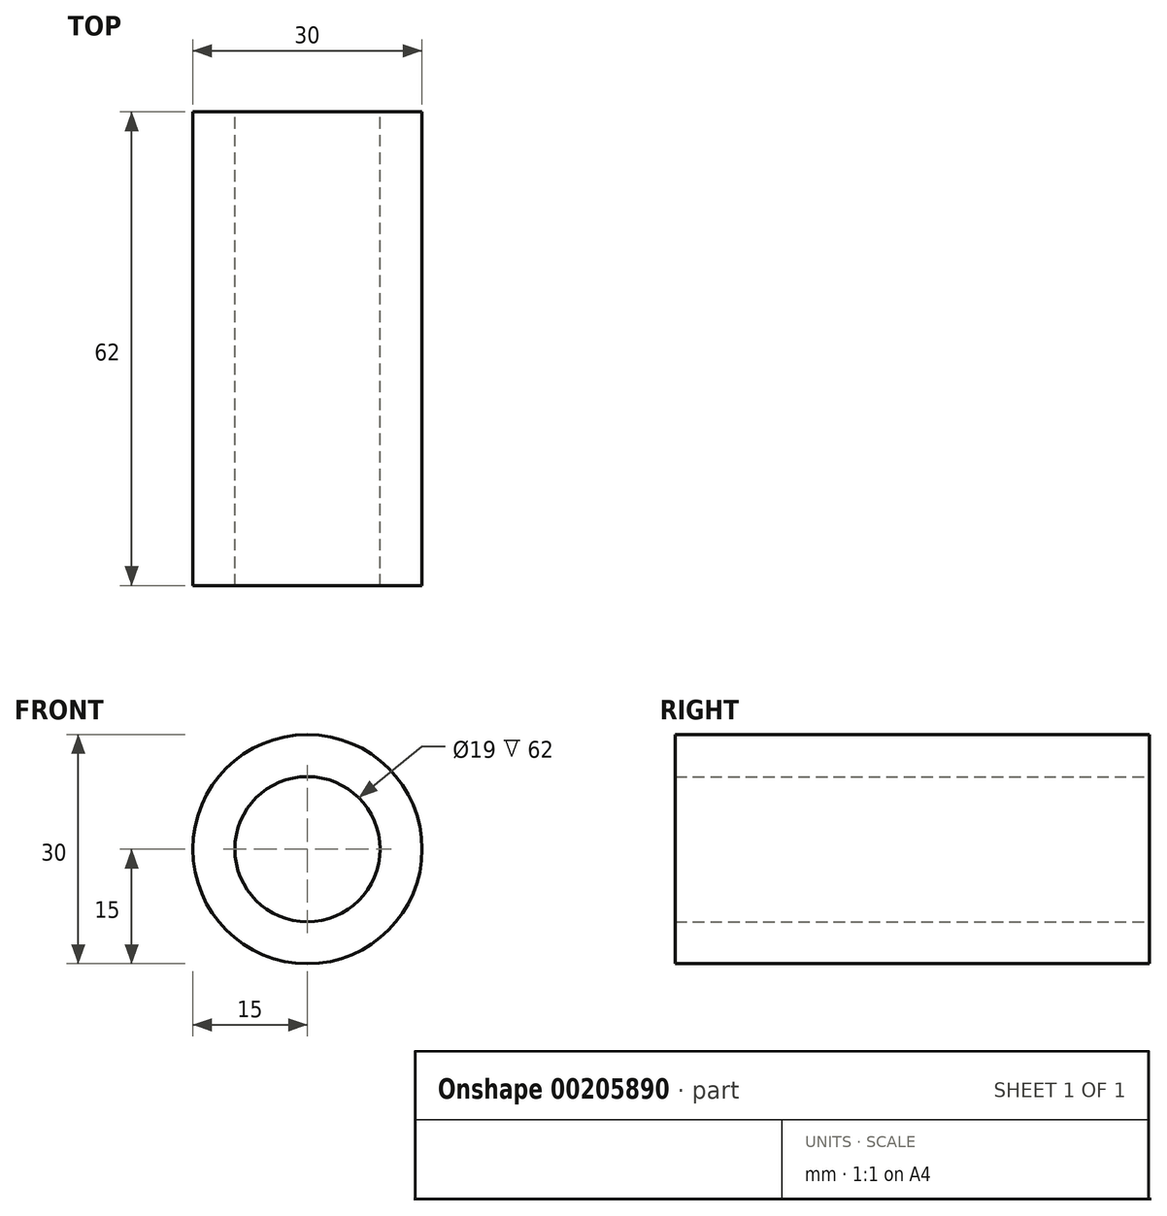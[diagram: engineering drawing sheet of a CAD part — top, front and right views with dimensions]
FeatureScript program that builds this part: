
annotation { "Feature Type Name" : "Feature", "Feature Type Description" : "" }
export const myFeature = defineFeature(function(context is Context, id is Id, definition is map)
    precondition{}
    {
        {
            var Q0;
            Q0=qCreatedBy(makeId("Front.planeOp"),FACE);
            var sketch = newSketch(context, id + "F0", { "sketchPlane" : qUnion([Q0])});
            skCircle(sketch, "E0", {"center": v(0, 0) * mm, "radius": 15 * mm});
            skCircle(sketch, "E1", {"center": v(0, 0) * mm, "radius": 9.5 * mm});
            skSolve(sketch);
        }
        {
            var Q0;
            Q0=makeQuery(id+"F0.imprint","IMPRINT",FACE,{"disambiguationData":[TD([[makeQuery(id+"F0.imprint","IMPRINT",EDGE,{"derivedFrom":sQuery(id+"F0.wireOp",EDGE,"E0")}),1.0]])]});
            extrude(context, id + "F1", {"entities" : qUnion([Q0]), "depth" : 62 * mm});
        }
    });
